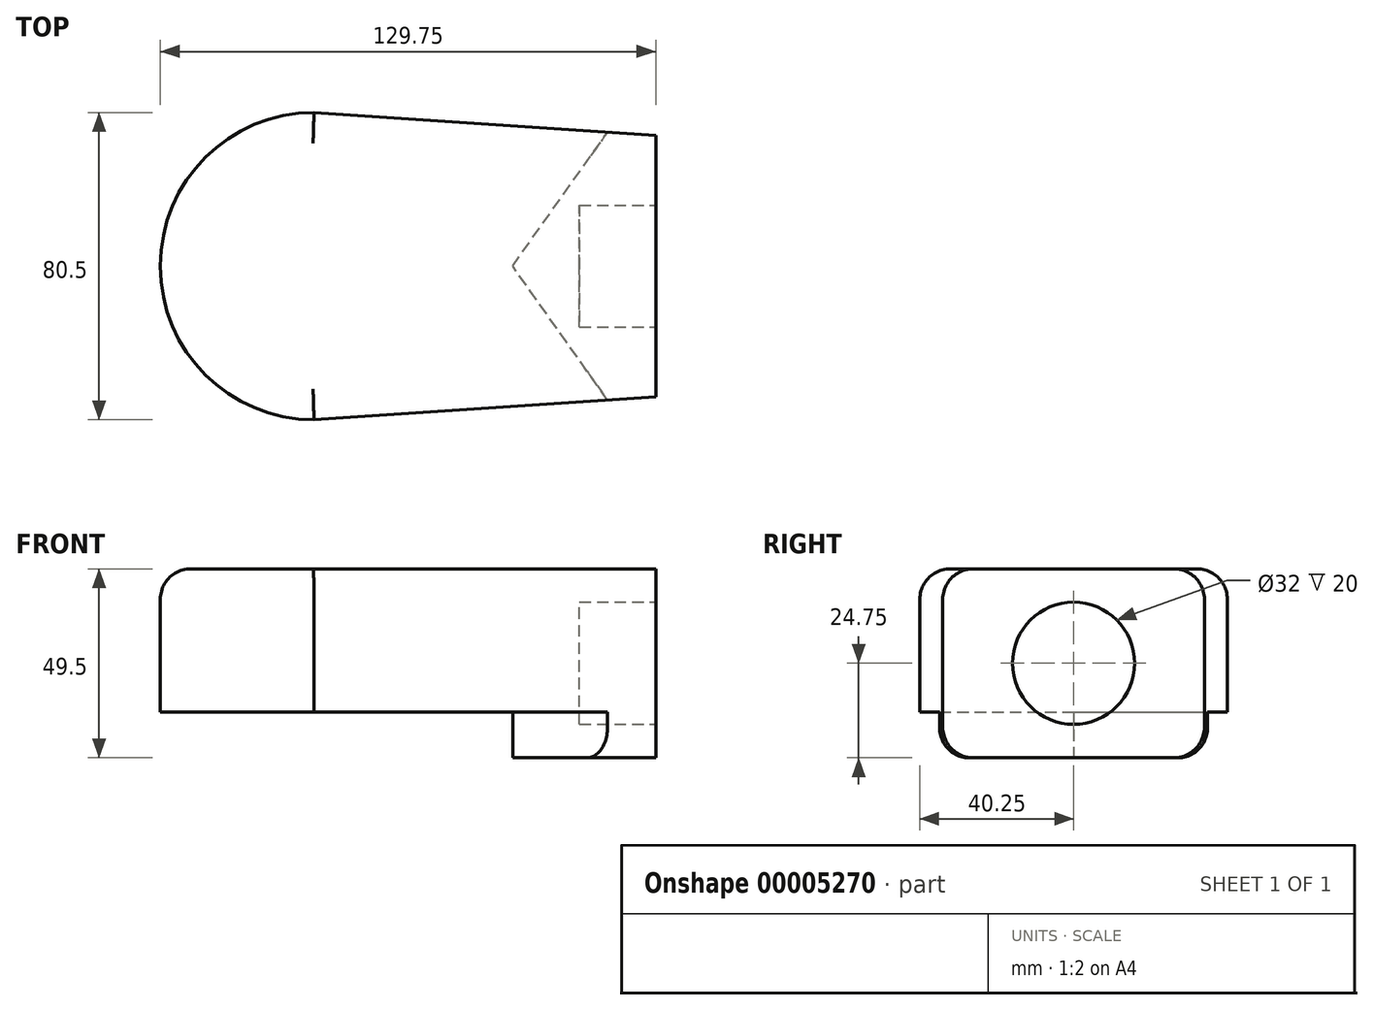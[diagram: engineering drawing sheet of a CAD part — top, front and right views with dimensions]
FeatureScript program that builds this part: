
annotation { "Feature Type Name" : "Feature", "Feature Type Description" : "" }
export const myFeature = defineFeature(function(context is Context, id is Id, definition is map)
    precondition{}
    {
        {
            var Q0;
            Q0=qCreatedBy(makeId("Top.planeOp"),FACE);
            var sketch = newSketch(context, id + "F0", { "sketchPlane" : qUnion([Q0])});
            skArc(sketch, "E0", {"start": v(0, 40.25) * mm, "mid": v(-40.25, 0) * mm, "end": v(0, -40.25) * mm});
            skLineSegment(sketch, "E1", {"start": v(0, 40.25) * mm, "end": v(89.5, 34.25) * mm});
            skLineSegment(sketch, "E2", {"start": v(89.5, 34.25) * mm, "end": v(89.5, -34.25) * mm});
            skLineSegment(sketch, "E3", {"start": v(89.5, -34.25) * mm, "end": v(0, -40.25) * mm});
            skPoint(sketch, "E4", {"position": v(89.5, 0) * mm});
            skSolve(sketch);
        }
        {
            var Q0;
            Q0=makeQuery(id+"F0.imprint","IMPRINT",FACE,{"disambiguationData":[TD([[makeQuery(id+"F0.imprint","IMPRINT",EDGE,{"derivedFrom":sQuery(id+"F0.wireOp",EDGE,"E0")}),1.0]])]});
            extrude(context, id + "F1", {"entities" : qUnion([Q0]), "depth" : 49.5 * mm});
        }
        {
            var Q0;
            Q0=makeQuery(id+"F1.opExtrude","CAP_FACE",FACE,{"disambiguationData":[OSD([sQuery(id+"F0.wireOp",EDGE,"E0"),sQuery(id+"F0.wireOp",EDGE,"E1"),sQuery(id+"F0.wireOp",EDGE,"E2"),sQuery(id+"F0.wireOp",EDGE,"E3")])],"isStart":true});
            var sketch = newSketch(context, id + "F2", { "sketchPlane" : qUnion([Q0])});
            skLineSegment(sketch, "E5", {"start": v(76.87, 35.1) * mm, "end": v(52, 0) * mm});
            skLineSegment(sketch, "E6", {"start": v(52, 0) * mm, "end": v(76.87, -35.1) * mm});
            skLineSegment(sketch, "E7", {"start": v(76.87, -35.1) * mm, "end": v(-48.5, -56.11) * mm});
            skLineSegment(sketch, "E8", {"start": v(-48.5, -56.11) * mm, "end": v(-51.9, 53.54) * mm});
            skLineSegment(sketch, "E9", {"start": v(-51.9, 53.54) * mm, "end": v(76.87, 35.1) * mm});
            skSolve(sketch);
        }
        {
            var Q0;
            {var subQ1=sQuery(id+"F2.wireOp",EDGE,"E5");var subQ7=sQuery(id+"F2.wireOp",EDGE,"E7");Q0=qUnion([makeQuery(id+"F2.imprint","IMPRINT",FACE,{"disambiguationData":[TD([[makeQuery(id+"F2.imprint","IMPRINT",EDGE,{"derivedFrom":subQ7}),-1.0]])]}),makeQuery(id+"F2.imprint","IMPRINT",FACE,{"disambiguationData":[TD([[makeQuery(id+"F2.imprint","IMPRINT",EDGE,{"derivedFrom":subQ1}),-1.0]])]})]);}
            extrude(context, id + "F3", {"entities" : qUnion([Q0]), "operationType" : NewBodyOperationType.REMOVE, "oppositeDirection" : true, "depth" : 12 * mm});
        }
        {
            var Q0;
            Q0=makeQuery(id+"F1.opExtrude","CAP_EDGE",EDGE,{"disambiguationData":[OSD([sQuery(id+"F0.wireOp",EDGE,"E1")])],"isStart":false});
            var Q1;
            Q1=makeQuery(id+"F1.opExtrude","CAP_EDGE",EDGE,{"disambiguationData":[OSD([sQuery(id+"F0.wireOp",EDGE,"E0")])],"isStart":false});
            var Q2;
            Q2=makeQuery(id+"F1.opExtrude","CAP_EDGE",EDGE,{"disambiguationData":[OSD([sQuery(id+"F0.wireOp",EDGE,"E3")])],"isStart":false});
            var Q3;
            Q3=makeQuery(id+"F1.opExtrude","CAP_EDGE",EDGE,{"disambiguationData":[OSD([sQuery(id+"F0.wireOp",EDGE,"E1")])],"isStart":true});
            var Q4;
            Q4=makeQuery(id+"F1.opExtrude","CAP_EDGE",EDGE,{"disambiguationData":[OSD([sQuery(id+"F0.wireOp",EDGE,"E3")])],"isStart":true});
            fillet(context, id + "F4", {"entities" : qUnion([Q0, Q1, Q2, Q3, Q4]), "radius" : 8 * mm, "tangentPropagation" : true, "allowEdgeOverflow" : false});
        }
        {
            var Q0;
            Q0=makeQuery(id+"F1.opExtrude","SWEPT_FACE",FACE,{"disambiguationData":[OSD([sQuery(id+"F0.wireOp",EDGE,"E2")])]});
            var sketch = newSketch(context, id + "F5", { "sketchPlane" : qUnion([Q0])});
            skCircle(sketch, "E10", {"center": v(0, 24.75) * mm, "radius": 16 * mm});
            skPoint(sketch, "E11", {"position": v(-34.25, 24.75) * mm});
            skPoint(sketch, "E12", {"position": v(0, 49.5) * mm});
            skSolve(sketch);
        }
        {
            var Q0;
            Q0=makeQuery(id+"F5.imprint","IMPRINT",FACE,{"disambiguationData":[TD([[makeQuery(id+"F5.imprint","IMPRINT",EDGE,{"derivedFrom":sQuery(id+"F5.wireOp",EDGE,"E10")}),1.0]])]});
            extrude(context, id + "F6", {"entities" : qUnion([Q0]), "operationType" : NewBodyOperationType.REMOVE, "oppositeDirection" : true, "depth" : 20 * mm});
        }
    });
